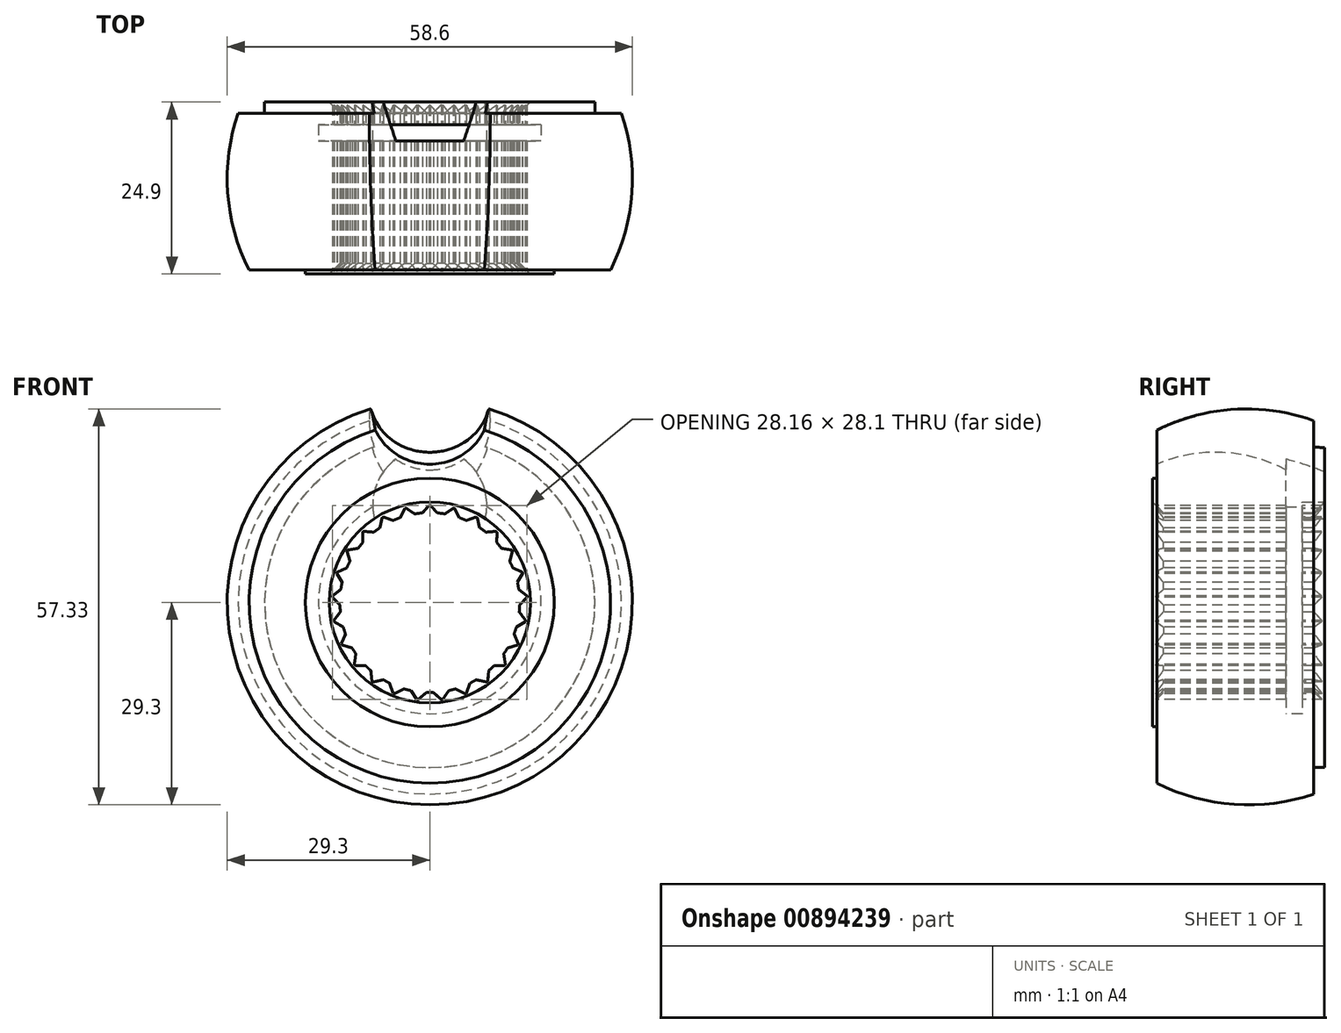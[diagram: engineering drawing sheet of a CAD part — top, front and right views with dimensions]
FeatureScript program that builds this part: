
annotation { "Feature Type Name" : "Feature", "Feature Type Description" : "" }
export const myFeature = defineFeature(function(context is Context, id is Id, definition is map)
    precondition{}
    {
        {
            var Q0;
            Q0=qCreatedBy(makeId("Right.planeOp"),FACE);
            var sketch = newSketch(context, id + "F0", { "sketchPlane" : qUnion([Q0])});
            skLineSegment(sketch, "E0", {"start": v(0, 14.55) * mm, "end": v(0, 18) * mm});
            skLineSegment(sketch, "E1", {"start": v(0, 18) * mm, "end": v(0.6, 18) * mm});
            skLineSegment(sketch, "E2", {"start": v(0.6, 18) * mm, "end": v(0.6, 26.15) * mm});
            skLineSegment(sketch, "E3", {"start": v(0, 14.55) * mm, "end": v(1.55, 13) * mm});
            skLineSegment(sketch, "E4", {"start": v(1.55, 13) * mm, "end": v(19.3, 13) * mm});
            skLineSegment(sketch, "E5", {"start": v(19.3, 13) * mm, "end": v(19.3, 16.1) * mm});
            skLineSegment(sketch, "E6", {"start": v(19.3, 16.1) * mm, "end": v(21.6, 16.1) * mm});
            skLineSegment(sketch, "E7", {"start": v(21.6, 16.1) * mm, "end": v(21.6, 13) * mm});
            skLineSegment(sketch, "E8", {"start": v(21.6, 13) * mm, "end": v(23.35, 13) * mm});
            skLineSegment(sketch, "E9", {"start": v(23.35, 13) * mm, "end": v(24.9, 14.55) * mm});
            skLineSegment(sketch, "E10", {"start": v(24.9, 14.55) * mm, "end": v(24.9, 23.9) * mm});
            skLineSegment(sketch, "E11", {"start": v(24.9, 23.9) * mm, "end": v(23.3, 23.9) * mm});
            skLineSegment(sketch, "E12", {"start": v(23.3, 23.9) * mm, "end": v(23.3, 27.73) * mm});
            skArc(sketch, "E13", {"start": v(23.3, 27.73) * mm, "mid": v(11.8, 29.23) * mm, "end": v(0.6, 26.15) * mm});
            skLineSegment(sketch, "E14", {"start": v(0, 0) * mm, "end": v(24.9, 0) * mm, "construction": true});
            skSolve(sketch);
        }
        {
            var Q0;
            Q0=makeQuery(id+"F0.imprint","IMPRINT",FACE,{"disambiguationData":[TD([[makeQuery(id+"F0.imprint","IMPRINT",EDGE,{"derivedFrom":sQuery(id+"F0.wireOp",EDGE,"E0")}),-1.0]])]});
            var Q1;
            Q1=sQuery(id+"F0.wireOp",EDGE,"E14");
            revolve(context, id + "F1", {"surfaceOperationType" : NewSurfaceOperationType.NEW, "entities" : qUnion([Q0]), "axis" : qUnion([Q1]), "revolveType" : RevolveType.FULL});
        }
        {
            var Q0;
            Q0=qCreatedBy(makeId("Front.planeOp"),FACE);
            var sketch = newSketch(context, id + "F2", { "sketchPlane" : qUnion([Q0])});
            skArc(sketch, "E15", {"start": v(1.63, 12.85) * mm, "mid": v(1.38, 12.88) * mm, "end": v(1.13, 12.9) * mm});
            skArc(sketch, "E16", {"start": v(0.1, 14.05) * mm, "mid": v(0.05, 14.05) * mm, "end": v(0, 14.05) * mm});
            skLineSegment(sketch, "E17", {"start": v(0.1, 14.05) * mm, "end": v(1.13, 12.9) * mm});
            skArc(sketch, "E18", {"start": v(-1.13, 12.9) * mm, "mid": v(-1.38, 12.88) * mm, "end": v(-1.63, 12.85) * mm});
            skArc(sketch, "E19", {"start": v(0, 14.05) * mm, "mid": v(-0.05, 14.05) * mm, "end": v(-0.1, 14.05) * mm});
            skLineSegment(sketch, "E20", {"start": v(-0.1, 14.05) * mm, "end": v(-1.13, 12.9) * mm});
            skArc(sketch, "E21", {"start": v(-1.63, 12.85) * mm, "mid": v(-1.88, 12.81) * mm, "end": v(-2.13, 12.78) * mm});
            skArc(sketch, "E22", {"start": v(-3.4, 13.63) * mm, "mid": v(-3.46, 13.62) * mm, "end": v(-3.5, 13.6) * mm});
            skLineSegment(sketch, "E23", {"start": v(-3.4, 13.63) * mm, "end": v(-2.13, 12.78) * mm});
            skArc(sketch, "E24", {"start": v(-4.31, 12.21) * mm, "mid": v(-4.55, 12.13) * mm, "end": v(-4.79, 12.04) * mm});
            skArc(sketch, "E25", {"start": v(-3.5, 13.6) * mm, "mid": v(-3.55, 13.6) * mm, "end": v(-3.6, 13.58) * mm});
            skLineSegment(sketch, "E26", {"start": v(-3.6, 13.58) * mm, "end": v(-4.31, 12.21) * mm});
            skArc(sketch, "E27", {"start": v(-4.79, 12.04) * mm, "mid": v(-5.02, 11.94) * mm, "end": v(-5.25, 11.84) * mm});
            skArc(sketch, "E28", {"start": v(-6.7, 12.35) * mm, "mid": v(-6.75, 12.33) * mm, "end": v(-6.8, 12.3) * mm});
            skLineSegment(sketch, "E29", {"start": v(-6.7, 12.35) * mm, "end": v(-5.25, 11.84) * mm});
            skArc(sketch, "E30", {"start": v(-7.23, 10.76) * mm, "mid": v(-7.44, 10.61) * mm, "end": v(-7.64, 10.47) * mm});
            skArc(sketch, "E31", {"start": v(-6.8, 12.3) * mm, "mid": v(-6.84, 12.28) * mm, "end": v(-6.88, 12.26) * mm});
            skLineSegment(sketch, "E32", {"start": v(-6.88, 12.26) * mm, "end": v(-7.23, 10.76) * mm});
            skArc(sketch, "E33", {"start": v(-7.64, 10.47) * mm, "mid": v(-7.84, 10.32) * mm, "end": v(-8.04, 10.16) * mm});
            skArc(sketch, "E34", {"start": v(-9.58, 10.3) * mm, "mid": v(-9.62, 10.26) * mm, "end": v(-9.65, 10.23) * mm});
            skLineSegment(sketch, "E35", {"start": v(-9.58, 10.3) * mm, "end": v(-8.04, 10.16) * mm});
            skArc(sketch, "E36", {"start": v(-9.69, 8.62) * mm, "mid": v(-9.85, 8.43) * mm, "end": v(-10.02, 8.24) * mm});
            skArc(sketch, "E37", {"start": v(-9.65, 10.23) * mm, "mid": v(-9.69, 10.2) * mm, "end": v(-9.72, 10.16) * mm});
            skLineSegment(sketch, "E38", {"start": v(-9.72, 10.16) * mm, "end": v(-9.69, 8.62) * mm});
            skArc(sketch, "E39", {"start": v(-10.02, 8.24) * mm, "mid": v(-10.18, 8.04) * mm, "end": v(-10.33, 7.84) * mm});
            skArc(sketch, "E40", {"start": v(-11.85, 7.59) * mm, "mid": v(-11.88, 7.55) * mm, "end": v(-11.9, 7.5) * mm});
            skLineSegment(sketch, "E41", {"start": v(-11.85, 7.59) * mm, "end": v(-10.33, 7.84) * mm});
            skArc(sketch, "E42", {"start": v(-11.54, 5.94) * mm, "mid": v(-11.65, 5.71) * mm, "end": v(-11.76, 5.49) * mm});
            skArc(sketch, "E43", {"start": v(-11.9, 7.5) * mm, "mid": v(-11.93, 7.46) * mm, "end": v(-11.96, 7.42) * mm});
            skLineSegment(sketch, "E44", {"start": v(-11.96, 7.42) * mm, "end": v(-11.54, 5.94) * mm});
            skArc(sketch, "E45", {"start": v(-11.76, 5.49) * mm, "mid": v(-11.87, 5.26) * mm, "end": v(-11.97, 5.03) * mm});
            skArc(sketch, "E46", {"start": v(-13.38, 4.4) * mm, "mid": v(-13.4, 4.36) * mm, "end": v(-13.4, 4.3) * mm});
            skLineSegment(sketch, "E47", {"start": v(-13.38, 4.4) * mm, "end": v(-11.97, 5.03) * mm});
            skArc(sketch, "E48", {"start": v(-12.67, 2.88) * mm, "mid": v(-12.72, 2.63) * mm, "end": v(-12.77, 2.39) * mm});
            skArc(sketch, "E49", {"start": v(-13.4, 4.3) * mm, "mid": v(-13.43, 4.26) * mm, "end": v(-13.44, 4.21) * mm});
            skLineSegment(sketch, "E50", {"start": v(-13.44, 4.21) * mm, "end": v(-12.67, 2.88) * mm});
            skArc(sketch, "E51", {"start": v(-12.77, 2.39) * mm, "mid": v(-12.81, 2.14) * mm, "end": v(-12.85, 1.89) * mm});
            skArc(sketch, "E52", {"start": v(-14.07, 0.94) * mm, "mid": v(-14.07, 0.89) * mm, "end": v(-14.07, 0.84) * mm});
            skLineSegment(sketch, "E53", {"start": v(-14.07, 0.94) * mm, "end": v(-12.85, 1.89) * mm});
            skArc(sketch, "E54", {"start": v(-13, -0.36) * mm, "mid": v(-12.99, -0.61) * mm, "end": v(-12.97, -0.87) * mm});
            skArc(sketch, "E55", {"start": v(-14.07, 0.84) * mm, "mid": v(-14.08, 0.79) * mm, "end": v(-14.08, 0.74) * mm});
            skLineSegment(sketch, "E56", {"start": v(-14.08, 0.74) * mm, "end": v(-13, -0.36) * mm});
            skArc(sketch, "E57", {"start": v(-12.97, -0.87) * mm, "mid": v(-12.96, -1.12) * mm, "end": v(-12.93, -1.37) * mm});
            skArc(sketch, "E58", {"start": v(-13.87, -2.6) * mm, "mid": v(-13.86, -2.64) * mm, "end": v(-13.85, -2.7) * mm});
            skLineSegment(sketch, "E59", {"start": v(-13.87, -2.6) * mm, "end": v(-12.93, -1.37) * mm});
            skArc(sketch, "E60", {"start": v(-12.51, -3.58) * mm, "mid": v(-12.44, -3.83) * mm, "end": v(-12.36, -4.07) * mm});
            skArc(sketch, "E61", {"start": v(-13.85, -2.7) * mm, "mid": v(-13.84, -2.74) * mm, "end": v(-13.83, -2.79) * mm});
            skLineSegment(sketch, "E62", {"start": v(-13.83, -2.79) * mm, "end": v(-12.51, -3.58) * mm});
            skArc(sketch, "E63", {"start": v(-12.36, -4.07) * mm, "mid": v(-12.28, -4.3) * mm, "end": v(-12.2, -4.54) * mm});
            skArc(sketch, "E64", {"start": v(-12.8, -5.96) * mm, "mid": v(-12.78, -6) * mm, "end": v(-12.76, -6.05) * mm});
            skLineSegment(sketch, "E65", {"start": v(-12.8, -5.96) * mm, "end": v(-12.2, -4.54) * mm});
            skArc(sketch, "E66", {"start": v(-11.24, -6.58) * mm, "mid": v(-11.1, -6.8) * mm, "end": v(-10.98, -7.02) * mm});
            skArc(sketch, "E67", {"start": v(-12.76, -6.05) * mm, "mid": v(-12.74, -6.1) * mm, "end": v(-12.72, -6.14) * mm});
            skLineSegment(sketch, "E68", {"start": v(-12.72, -6.14) * mm, "end": v(-11.24, -6.58) * mm});
            skArc(sketch, "E69", {"start": v(-10.98, -7.02) * mm, "mid": v(-10.84, -7.23) * mm, "end": v(-10.7, -7.44) * mm});
            skArc(sketch, "E70", {"start": v(-10.93, -8.96) * mm, "mid": v(-10.9, -9) * mm, "end": v(-10.86, -9.04) * mm});
            skLineSegment(sketch, "E71", {"start": v(-10.93, -8.96) * mm, "end": v(-10.7, -7.44) * mm});
            skArc(sketch, "E72", {"start": v(-9.26, -9.17) * mm, "mid": v(-9.08, -9.35) * mm, "end": v(-8.9, -9.53) * mm});
            skArc(sketch, "E73", {"start": v(-10.86, -9.04) * mm, "mid": v(-10.83, -9.08) * mm, "end": v(-10.8, -9.11) * mm});
            skLineSegment(sketch, "E74", {"start": v(-10.8, -9.11) * mm, "end": v(-9.26, -9.17) * mm});
            skArc(sketch, "E75", {"start": v(-8.9, -9.53) * mm, "mid": v(-8.71, -9.7) * mm, "end": v(-8.53, -9.86) * mm});
            skArc(sketch, "E76", {"start": v(-8.37, -11.4) * mm, "mid": v(-8.33, -11.43) * mm, "end": v(-8.29, -11.46) * mm});
            skLineSegment(sketch, "E77", {"start": v(-8.37, -11.4) * mm, "end": v(-8.53, -9.86) * mm});
            skArc(sketch, "E78", {"start": v(-6.7, -11.2) * mm, "mid": v(-6.48, -11.32) * mm, "end": v(-6.26, -11.44) * mm});
            skArc(sketch, "E79", {"start": v(-8.29, -11.46) * mm, "mid": v(-8.25, -11.49) * mm, "end": v(-8.2, -11.52) * mm});
            skLineSegment(sketch, "E80", {"start": v(-8.2, -11.52) * mm, "end": v(-6.7, -11.2) * mm});
            skArc(sketch, "E81", {"start": v(-6.26, -11.44) * mm, "mid": v(-6.04, -11.56) * mm, "end": v(-5.82, -11.68) * mm});
            skArc(sketch, "E82", {"start": v(-5.28, -13.12) * mm, "mid": v(-5.24, -13.14) * mm, "end": v(-5.2, -13.16) * mm});
            skLineSegment(sketch, "E83", {"start": v(-5.28, -13.12) * mm, "end": v(-5.82, -11.68) * mm});
            skArc(sketch, "E84", {"start": v(-3.72, -12.5) * mm, "mid": v(-3.48, -12.58) * mm, "end": v(-3.23, -12.64) * mm});
            skArc(sketch, "E85", {"start": v(-5.2, -13.16) * mm, "mid": v(-5.14, -13.18) * mm, "end": v(-5.1, -13.2) * mm});
            skLineSegment(sketch, "E86", {"start": v(-5.1, -13.2) * mm, "end": v(-3.72, -12.5) * mm});
            skArc(sketch, "E87", {"start": v(-3.23, -12.64) * mm, "mid": v(-2.99, -12.7) * mm, "end": v(-2.74, -12.76) * mm});
            skArc(sketch, "E88", {"start": v(-1.87, -14.03) * mm, "mid": v(-1.82, -14.03) * mm, "end": v(-1.77, -14.04) * mm});
            skLineSegment(sketch, "E89", {"start": v(-1.87, -14.03) * mm, "end": v(-2.74, -12.76) * mm});
            skArc(sketch, "E90", {"start": v(-0.5, -13.04) * mm, "mid": v(-0.25, -13.05) * mm, "end": v(0, -13.05) * mm});
            skArc(sketch, "E91", {"start": v(-1.77, -14.04) * mm, "mid": v(-1.72, -14.04) * mm, "end": v(-1.67, -14.05) * mm});
            skLineSegment(sketch, "E92", {"start": v(-1.67, -14.05) * mm, "end": v(-0.5, -13.04) * mm});
            skArc(sketch, "E93", {"start": v(0, -13.05) * mm, "mid": v(0.25, -13.05) * mm, "end": v(0.5, -13.04) * mm});
            skArc(sketch, "E94", {"start": v(1.67, -14.05) * mm, "mid": v(1.72, -14.04) * mm, "end": v(1.77, -14.04) * mm});
            skLineSegment(sketch, "E95", {"start": v(1.67, -14.05) * mm, "end": v(0.5, -13.04) * mm});
            skArc(sketch, "E96", {"start": v(2.74, -12.76) * mm, "mid": v(2.99, -12.7) * mm, "end": v(3.23, -12.64) * mm});
            skArc(sketch, "E97", {"start": v(1.77, -14.04) * mm, "mid": v(1.82, -14.03) * mm, "end": v(1.87, -14.03) * mm});
            skLineSegment(sketch, "E98", {"start": v(1.87, -14.03) * mm, "end": v(2.74, -12.76) * mm});
            skArc(sketch, "E99", {"start": v(3.23, -12.64) * mm, "mid": v(3.48, -12.58) * mm, "end": v(3.72, -12.5) * mm});
            skArc(sketch, "E100", {"start": v(5.1, -13.2) * mm, "mid": v(5.14, -13.18) * mm, "end": v(5.2, -13.16) * mm});
            skLineSegment(sketch, "E101", {"start": v(5.1, -13.2) * mm, "end": v(3.72, -12.5) * mm});
            skArc(sketch, "E102", {"start": v(5.82, -11.68) * mm, "mid": v(6.04, -11.56) * mm, "end": v(6.26, -11.44) * mm});
            skArc(sketch, "E103", {"start": v(5.2, -13.16) * mm, "mid": v(5.24, -13.14) * mm, "end": v(5.28, -13.12) * mm});
            skLineSegment(sketch, "E104", {"start": v(5.28, -13.12) * mm, "end": v(5.82, -11.68) * mm});
            skArc(sketch, "E105", {"start": v(6.26, -11.44) * mm, "mid": v(6.48, -11.32) * mm, "end": v(6.7, -11.2) * mm});
            skArc(sketch, "E106", {"start": v(8.2, -11.52) * mm, "mid": v(8.25, -11.49) * mm, "end": v(8.29, -11.46) * mm});
            skLineSegment(sketch, "E107", {"start": v(8.2, -11.52) * mm, "end": v(6.7, -11.2) * mm});
            skArc(sketch, "E108", {"start": v(8.53, -9.86) * mm, "mid": v(8.71, -9.7) * mm, "end": v(8.9, -9.53) * mm});
            skArc(sketch, "E109", {"start": v(8.29, -11.46) * mm, "mid": v(8.33, -11.43) * mm, "end": v(8.37, -11.4) * mm});
            skLineSegment(sketch, "E110", {"start": v(8.37, -11.4) * mm, "end": v(8.53, -9.86) * mm});
            skArc(sketch, "E111", {"start": v(8.9, -9.53) * mm, "mid": v(9.08, -9.35) * mm, "end": v(9.26, -9.17) * mm});
            skArc(sketch, "E112", {"start": v(10.8, -9.11) * mm, "mid": v(10.83, -9.08) * mm, "end": v(10.86, -9.04) * mm});
            skLineSegment(sketch, "E113", {"start": v(10.8, -9.11) * mm, "end": v(9.26, -9.17) * mm});
            skArc(sketch, "E114", {"start": v(10.7, -7.44) * mm, "mid": v(10.84, -7.23) * mm, "end": v(10.98, -7.02) * mm});
            skArc(sketch, "E115", {"start": v(10.86, -9.04) * mm, "mid": v(10.9, -9) * mm, "end": v(10.93, -8.96) * mm});
            skLineSegment(sketch, "E116", {"start": v(10.93, -8.96) * mm, "end": v(10.7, -7.44) * mm});
            skArc(sketch, "E117", {"start": v(10.98, -7.02) * mm, "mid": v(11.1, -6.8) * mm, "end": v(11.24, -6.58) * mm});
            skArc(sketch, "E118", {"start": v(12.72, -6.14) * mm, "mid": v(12.74, -6.1) * mm, "end": v(12.76, -6.05) * mm});
            skLineSegment(sketch, "E119", {"start": v(12.72, -6.14) * mm, "end": v(11.24, -6.58) * mm});
            skArc(sketch, "E120", {"start": v(12.2, -4.54) * mm, "mid": v(12.28, -4.3) * mm, "end": v(12.36, -4.07) * mm});
            skArc(sketch, "E121", {"start": v(12.76, -6.05) * mm, "mid": v(12.78, -6) * mm, "end": v(12.8, -5.96) * mm});
            skLineSegment(sketch, "E122", {"start": v(12.8, -5.96) * mm, "end": v(12.2, -4.54) * mm});
            skArc(sketch, "E123", {"start": v(12.36, -4.07) * mm, "mid": v(12.44, -3.83) * mm, "end": v(12.51, -3.58) * mm});
            skArc(sketch, "E124", {"start": v(13.83, -2.79) * mm, "mid": v(13.84, -2.74) * mm, "end": v(13.85, -2.7) * mm});
            skLineSegment(sketch, "E125", {"start": v(13.83, -2.79) * mm, "end": v(12.51, -3.58) * mm});
            skArc(sketch, "E126", {"start": v(12.93, -1.37) * mm, "mid": v(12.96, -1.12) * mm, "end": v(12.97, -0.87) * mm});
            skArc(sketch, "E127", {"start": v(13.85, -2.7) * mm, "mid": v(13.86, -2.64) * mm, "end": v(13.87, -2.6) * mm});
            skLineSegment(sketch, "E128", {"start": v(13.87, -2.6) * mm, "end": v(12.93, -1.37) * mm});
            skArc(sketch, "E129", {"start": v(12.97, -0.87) * mm, "mid": v(12.99, -0.61) * mm, "end": v(13, -0.36) * mm});
            skArc(sketch, "E130", {"start": v(14.08, 0.74) * mm, "mid": v(14.08, 0.79) * mm, "end": v(14.07, 0.84) * mm});
            skLineSegment(sketch, "E131", {"start": v(14.08, 0.74) * mm, "end": v(13, -0.36) * mm});
            skArc(sketch, "E132", {"start": v(12.85, 1.89) * mm, "mid": v(12.81, 2.14) * mm, "end": v(12.77, 2.39) * mm});
            skArc(sketch, "E133", {"start": v(14.07, 0.84) * mm, "mid": v(14.07, 0.89) * mm, "end": v(14.07, 0.94) * mm});
            skLineSegment(sketch, "E134", {"start": v(14.07, 0.94) * mm, "end": v(12.85, 1.89) * mm});
            skArc(sketch, "E135", {"start": v(12.77, 2.39) * mm, "mid": v(12.72, 2.63) * mm, "end": v(12.67, 2.88) * mm});
            skArc(sketch, "E136", {"start": v(13.44, 4.21) * mm, "mid": v(13.43, 4.26) * mm, "end": v(13.4, 4.3) * mm});
            skLineSegment(sketch, "E137", {"start": v(13.44, 4.21) * mm, "end": v(12.67, 2.88) * mm});
            skArc(sketch, "E138", {"start": v(11.97, 5.03) * mm, "mid": v(11.87, 5.26) * mm, "end": v(11.76, 5.49) * mm});
            skArc(sketch, "E139", {"start": v(13.4, 4.3) * mm, "mid": v(13.4, 4.36) * mm, "end": v(13.38, 4.4) * mm});
            skLineSegment(sketch, "E140", {"start": v(13.38, 4.4) * mm, "end": v(11.97, 5.03) * mm});
            skArc(sketch, "E141", {"start": v(11.76, 5.49) * mm, "mid": v(11.65, 5.71) * mm, "end": v(11.54, 5.94) * mm});
            skArc(sketch, "E142", {"start": v(11.96, 7.42) * mm, "mid": v(11.93, 7.46) * mm, "end": v(11.9, 7.5) * mm});
            skLineSegment(sketch, "E143", {"start": v(11.96, 7.42) * mm, "end": v(11.54, 5.94) * mm});
            skArc(sketch, "E144", {"start": v(10.33, 7.84) * mm, "mid": v(10.18, 8.04) * mm, "end": v(10.02, 8.24) * mm});
            skArc(sketch, "E145", {"start": v(11.9, 7.5) * mm, "mid": v(11.88, 7.55) * mm, "end": v(11.85, 7.59) * mm});
            skLineSegment(sketch, "E146", {"start": v(11.85, 7.59) * mm, "end": v(10.33, 7.84) * mm});
            skArc(sketch, "E147", {"start": v(10.02, 8.24) * mm, "mid": v(9.85, 8.43) * mm, "end": v(9.69, 8.62) * mm});
            skArc(sketch, "E148", {"start": v(9.72, 10.16) * mm, "mid": v(9.69, 10.2) * mm, "end": v(9.65, 10.23) * mm});
            skLineSegment(sketch, "E149", {"start": v(9.72, 10.16) * mm, "end": v(9.69, 8.62) * mm});
            skArc(sketch, "E150", {"start": v(8.04, 10.16) * mm, "mid": v(7.84, 10.32) * mm, "end": v(7.64, 10.47) * mm});
            skArc(sketch, "E151", {"start": v(9.65, 10.23) * mm, "mid": v(9.62, 10.26) * mm, "end": v(9.58, 10.3) * mm});
            skLineSegment(sketch, "E152", {"start": v(9.58, 10.3) * mm, "end": v(8.04, 10.16) * mm});
            skArc(sketch, "E153", {"start": v(7.64, 10.47) * mm, "mid": v(7.44, 10.61) * mm, "end": v(7.23, 10.76) * mm});
            skArc(sketch, "E154", {"start": v(6.88, 12.26) * mm, "mid": v(6.84, 12.28) * mm, "end": v(6.8, 12.3) * mm});
            skLineSegment(sketch, "E155", {"start": v(6.88, 12.26) * mm, "end": v(7.23, 10.76) * mm});
            skArc(sketch, "E156", {"start": v(5.25, 11.84) * mm, "mid": v(5.02, 11.94) * mm, "end": v(4.79, 12.04) * mm});
            skArc(sketch, "E157", {"start": v(6.8, 12.3) * mm, "mid": v(6.75, 12.33) * mm, "end": v(6.7, 12.35) * mm});
            skLineSegment(sketch, "E158", {"start": v(6.7, 12.35) * mm, "end": v(5.25, 11.84) * mm});
            skArc(sketch, "E159", {"start": v(4.79, 12.04) * mm, "mid": v(4.55, 12.13) * mm, "end": v(4.31, 12.21) * mm});
            skArc(sketch, "E160", {"start": v(3.6, 13.58) * mm, "mid": v(3.55, 13.6) * mm, "end": v(3.5, 13.6) * mm});
            skLineSegment(sketch, "E161", {"start": v(3.6, 13.58) * mm, "end": v(4.31, 12.21) * mm});
            skArc(sketch, "E162", {"start": v(2.13, 12.78) * mm, "mid": v(1.88, 12.81) * mm, "end": v(1.63, 12.85) * mm});
            skArc(sketch, "E163", {"start": v(3.5, 13.6) * mm, "mid": v(3.46, 13.62) * mm, "end": v(3.4, 13.63) * mm});
            skLineSegment(sketch, "E164", {"start": v(3.4, 13.63) * mm, "end": v(2.13, 12.78) * mm});
            skCircle(sketch, "E165", {"center": v(0, 0) * mm, "radius": 11.94 * mm});
            skSolve(sketch);
        }
        {
            var Q0;
            Q0=makeQuery(id+"F2.imprint","IMPRINT",FACE,{"disambiguationData":[TD([[makeQuery(id+"F2.imprint","IMPRINT",EDGE,{"derivedFrom":sQuery(id+"F2.wireOp",EDGE,"E15")}),1.0]])]});
            var Q1;
            Q1=sQuery(id+"F2.wireOp",EDGE,"E165");
            extrude(context, id + "F3", {"entities" : qUnion([Q0]), "operationType" : NewBodyOperationType.REMOVE, "surfaceEntities" : qUnion([Q1]), "endBound" : BoundingType.THROUGH_ALL, "oppositeDirection" : true, "depth" : 25 * mm, "offsetDistance" : 25 * mm});
        }
        {
            var Q0;
            Q0=qCreatedBy(makeId("Right.planeOp"),FACE);
            var sketch = newSketch(context, id + "F4", { "sketchPlane" : qUnion([Q0])});
            skArc(sketch, "E166", {"start": v(24.9, 14.55) * mm, "mid": v(13.58, 21.02) * mm, "end": v(0.6, 19.75) * mm});
            skSolve(sketch);
        }
        {
            var Q0;
            Q0=qCreatedBy(makeId("Front.planeOp"),FACE);
            var sketch = newSketch(context, id + "F5", { "sketchPlane" : qUnion([Q0])});
            skArc(sketch, "E167", {"start": v(0, 19.75) * mm, "mid": v(8.75, 28.5) * mm, "end": v(0, 37.25) * mm});
            skLineSegment(sketch, "E168", {"start": v(0, 37.25) * mm, "end": v(0, 19.75) * mm});
            skSolve(sketch);
        }
        {
            var Q0;
            Q0=makeQuery(id+"F5.imprint","IMPRINT",FACE,{"disambiguationData":[TD([[makeQuery(id+"F5.imprint","IMPRINT",EDGE,{"derivedFrom":sQuery(id+"F5.wireOp",EDGE,"E167")}),1.0]])]});
            var Q1;
            Q1=sQuery(id+"F4.wireOp",EDGE,"E166");
            sweep(context, id + "F6", {"operationType" : NewBodyOperationType.REMOVE, "profiles" : qUnion([Q0]), "path" : qUnion([Q1])});
        }
        {
            var Q0;
            Q0=makeQuery(id+"F1.opRevolve","SWEPT_FACE",FACE,{"disambiguationData":[OSD([sQuery(id+"F0.wireOp",EDGE,"E10")])]});
            var sketch = newSketch(context, id + "F7", { "sketchPlane" : qUnion([Q0])});
            skCircle(sketch, "E169", {"center": v(0, 14.1) * mm, "radius": 8.25 * mm});
            skSolve(sketch);
        }
        {
            var Q0;
            {var subQ0=sQuery(id+"F5.wireOp",EDGE,"svW5wT8A-36YJ-ZffP-jfzL-LTaveh01zYD9");var subQ2=sQuery(id+"F0.wireOp",EDGE,"E10");var subQ3=makeQuery(id+"F1.opRevolve","SWEPT_FACE",FACE,{"disambiguationData":[OSD([subQ2])]});var subQ5=makeQuery(id+"F6.boolean.opBoolean","INTERSECT",EDGE,{"derivedFrom":[subQ3,makeQuery(id+"F6.opSweep","CAP_FACE",FACE,{"disambiguationData":[OSD([sQuery(id+"F4.wireOp",VERTEX,"E166.start"),subQ0])],"isStart":false})]});Q0=makeQuery(id+"F7.imprint","IMPRINT",FACE,{"disambiguationData":[TD([[makeQuery(id+"F7.imprint","IMPRINT",EDGE,{"derivedFrom":subQ5}),-1.0]])]});}
            var Q1;
            {var subQ1=sQuery(id+"F5.wireOp",EDGE,"svW5wT8A-36YJ-ZffP-jfzL-LTaveh01zYD9");var subQ3=makeQuery(id+"F1.opRevolve","SWEPT_FACE",FACE,{"disambiguationData":[OSD([sQuery(id+"F0.wireOp",EDGE,"E10")])]});var subQ8=makeQuery(id+"F6.boolean.opBoolean","INTERSECT",EDGE,{"derivedFrom":[subQ3,makeQuery(id+"F6.opSweep","CAP_FACE",FACE,{"disambiguationData":[OSD([sQuery(id+"F4.wireOp",VERTEX,"E166.start"),subQ1])],"isStart":false})]});Q1=makeQuery(id+"F7.imprint","IMPRINT",FACE,{"disambiguationData":[TD([[makeQuery(id+"F7.imprint","IMPRINT",EDGE,{"derivedFrom":subQ8}),1.0]])]});}
            var Q2;
            {var subQ0=sQuery(id+"F7.wireOp",EDGE,"E169");var subQ1=makeQuery(id+"F1.opRevolve","SWEPT_EDGE",EDGE,{"disambiguationData":[OSD([sQuery(id+"F0.wireOp",EDGE,"E9"),sQuery(id+"F0.wireOp",EDGE,"E10")])]});var subQ2=makeQuery(id+"F7.imprint","INTERSECT",VERTEX,{"disambiguationData":[OD(0.0)],"derivedFrom":[subQ1,subQ0]});Q2=makeQuery(id+"F7.imprint","IMPRINT",FACE,{"disambiguationData":[TD([[makeQuery(id+"F7.imprint","IMPRINT",EDGE,{"disambiguationData":[TD([[subQ2,-1.0]])],"derivedFrom":subQ0}),1.0]])]});}
            extrude(context, id + "F8", {"entities" : qUnion([Q0, Q1, Q2]), "operationType" : NewBodyOperationType.REMOVE, "oppositeDirection" : true, "depth" : 5.6 * mm, "offsetDistance" : 25 * mm});
        }
        {
            var Q0;
            Q0=qCreatedBy(makeId("Front.planeOp"),FACE);
            var sketch = newSketch(context, id + "F9", { "sketchPlane" : qUnion([Q0])});
            skArc(sketch, "E170", {"start": v(0, 37.25) * mm, "mid": v(-8.75, 28.5) * mm, "end": v(0, 19.75) * mm});
            skLineSegment(sketch, "E171", {"start": v(0, 37.25) * mm, "end": v(0, 28.5) * mm});
            skLineSegment(sketch, "E172", {"start": v(0, 19.75) * mm, "end": v(0, 28.5) * mm});
            skSolve(sketch);
        }
        {
            var Q0;
            Q0=makeQuery(id+"F9.imprint","IMPRINT",FACE,{"disambiguationData":[TD([[makeQuery(id+"F9.imprint","IMPRINT",EDGE,{"derivedFrom":sQuery(id+"F9.wireOp",EDGE,"E170")}),1.0]])]});
            var Q1;
            Q1 = qConstructionFilter(qBodyType(qCreatedBy(id + "F4" ,EDGE), BodyType.WIRE), ConstructionObject.NO);
            sweep(context, id + "F10", {"operationType" : NewBodyOperationType.REMOVE, "profiles" : qUnion([Q0]), "path" : qUnion([Q1])});
        }
    });
